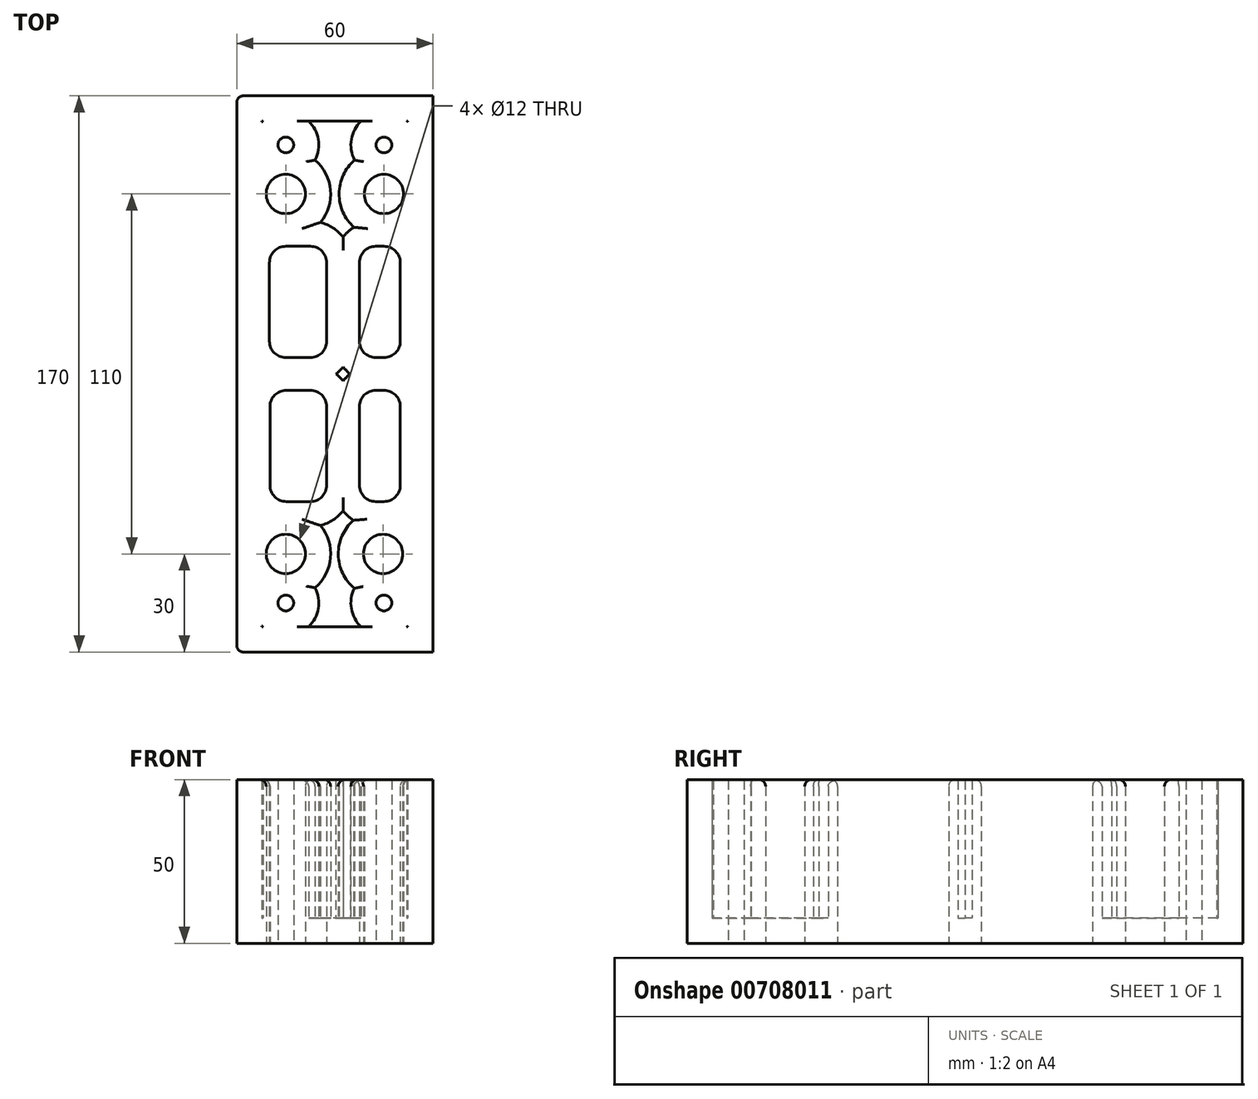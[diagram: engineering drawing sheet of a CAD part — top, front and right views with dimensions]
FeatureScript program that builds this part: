
annotation { "Feature Type Name" : "Feature", "Feature Type Description" : "" }
export const myFeature = defineFeature(function(context is Context, id is Id, definition is map)
    precondition{}
    {
        {
            var Q0;
            Q0=qCreatedBy(makeId("Top.planeOp"),FACE);
            var sketch = newSketch(context, id + "F0", { "sketchPlane" : qUnion([Q0])});
            skLineSegment(sketch, "E0.bottom", {"start": v(0, 0) * mm, "end": v(-55, 0) * mm});
            skLineSegment(sketch, "E0.top", {"start": v(0, 170) * mm, "end": v(-55, 170) * mm});
            skLineSegment(sketch, "E0.left", {"start": v(0, 0) * mm, "end": v(0, 170) * mm});
            skLineSegment(sketch, "E1.bottom", {"start": v(-55, 0) * mm, "end": v(-60, 0) * mm});
            skLineSegment(sketch, "E1.top", {"start": v(-55, 170) * mm, "end": v(-60, 170) * mm});
            skLineSegment(sketch, "E1.right", {"start": v(-60, 0) * mm, "end": v(-60, 170) * mm});
            skLineSegment(sketch, "E2.bottom", {"start": v(-55, 170) * mm, "end": v(-45, 170) * mm});
            skLineSegment(sketch, "E2.top", {"start": v(-60, 155) * mm, "end": v(-45, 155) * mm, "construction": true});
            skLineSegment(sketch, "E2.right", {"start": v(-45, 170) * mm, "end": v(-45, 155) * mm, "construction": true});
            skLineSegment(sketch, "E3.bottom", {"start": v(0, 170) * mm, "end": v(-15, 170) * mm});
            skLineSegment(sketch, "E3.top", {"start": v(0, 155) * mm, "end": v(-15, 155) * mm, "construction": true});
            skLineSegment(sketch, "E3.left", {"start": v(0, 170) * mm, "end": v(0, 155) * mm});
            skLineSegment(sketch, "E3.right", {"start": v(-15, 170) * mm, "end": v(-15, 155) * mm, "construction": true});
            skLineSegment(sketch, "E4.bottom", {"start": v(0, 0) * mm, "end": v(-15, 0) * mm});
            skLineSegment(sketch, "E4.top", {"start": v(0, 15) * mm, "end": v(-15, 15) * mm, "construction": true});
            skLineSegment(sketch, "E4.left", {"start": v(0, 0) * mm, "end": v(0, 15) * mm});
            skLineSegment(sketch, "E4.right", {"start": v(-15, 0) * mm, "end": v(-15, 15) * mm, "construction": true});
            skLineSegment(sketch, "E5.bottom", {"start": v(-55, 0) * mm, "end": v(-45, 0) * mm});
            skLineSegment(sketch, "E5.top", {"start": v(-55, 15) * mm, "end": v(-45, 15) * mm, "construction": true});
            skLineSegment(sketch, "E5.right", {"start": v(-45, 0) * mm, "end": v(-45, 15) * mm, "construction": true});
            skCircle(sketch, "E6", {"center": v(-45, 15) * mm, "radius": 2.4 * mm});
            skCircle(sketch, "E7", {"center": v(-15, 15) * mm, "radius": 2.4 * mm});
            skCircle(sketch, "E8", {"center": v(-15, 155) * mm, "radius": 2.4 * mm});
            skCircle(sketch, "E9", {"center": v(-45, 155) * mm, "radius": 2.4 * mm});
            skLineSegment(sketch, "E10", {"start": v(-45, 155) * mm, "end": v(-45, 140) * mm, "construction": true});
            skLineSegment(sketch, "E11", {"start": v(-15, 155) * mm, "end": v(-15, 140) * mm, "construction": true});
            skLineSegment(sketch, "E12", {"start": v(-45, 15) * mm, "end": v(-45, 30) * mm, "construction": true});
            skLineSegment(sketch, "E13", {"start": v(-15, 15) * mm, "end": v(-15.26, 30) * mm, "construction": true});
            skCircle(sketch, "E14", {"center": v(-45, 30) * mm, "radius": 6 * mm});
            skCircle(sketch, "E15", {"center": v(-15.26, 30) * mm, "radius": 6 * mm});
            skCircle(sketch, "E16", {"center": v(-45, 140) * mm, "radius": 6 * mm});
            skCircle(sketch, "E17", {"center": v(-15, 140) * mm, "radius": 6 * mm});
            skLineSegment(sketch, "E18", {"start": v(-27.5, 170) * mm, "end": v(-27.5, 0) * mm, "construction": true});
            skLineSegment(sketch, "E19.0", {"start": v(-32.5, 119) * mm, "end": v(-32.5, 95) * mm});
            skLineSegment(sketch, "E20.0", {"start": v(-22.5, 119) * mm, "end": v(-22.5, 95) * mm});
            skLineSegment(sketch, "E21", {"start": v(-55, 85) * mm, "end": v(0, 85) * mm, "construction": true});
            skLineSegment(sketch, "E22.0", {"start": v(-44.84, 80) * mm, "end": v(-37.5, 80) * mm});
            skLineSegment(sketch, "E23.0", {"start": v(-45, 90) * mm, "end": v(-37.5, 90) * mm});
            skLineSegment(sketch, "E24.trimOffspring", {"start": v(-17.5, 90) * mm, "end": v(-15, 90) * mm});
            skLineSegment(sketch, "E25.trimOffspring", {"start": v(-22.5, 75) * mm, "end": v(-22.5, 51) * mm});
            skLineSegment(sketch, "E26.trimOffspring", {"start": v(-17.5, 80) * mm, "end": v(-15, 80) * mm});
            skLineSegment(sketch, "E27.trimOffspring", {"start": v(-32.5, 75) * mm, "end": v(-32.5, 51) * mm});
            skLineSegment(sketch, "E28", {"start": v(-44.66, 134) * mm, "end": v(-44.66, 124) * mm, "construction": true});
            skLineSegment(sketch, "E29", {"start": v(-44.73, 36) * mm, "end": v(-44.73, 46) * mm, "construction": true});
            skLineSegment(sketch, "E30", {"start": v(-44.84, 46) * mm, "end": v(-37.5, 46) * mm});
            skLineSegment(sketch, "E31", {"start": v(-45, 124) * mm, "end": v(-37.5, 124) * mm});
            skLineSegment(sketch, "E32.trimOffspring", {"start": v(-17.5, 124) * mm, "end": v(-15, 124) * mm});
            skPoint(sketch, "E33.start.orphan", {"position": v(-15.26, 36) * mm});
            skLineSegment(sketch, "E34.trimOffspring", {"start": v(-17.5, 46) * mm, "end": v(-15, 46) * mm});
            skPoint(sketch, "E35.orphan", {"position": v(-55, 124) * mm});
            skPoint(sketch, "E36.orphan", {"position": v(-54.84, 46) * mm});
            skLineSegment(sketch, "E37.trimOffspring", {"start": v(-50, 95) * mm, "end": v(-50, 119) * mm});
            skLineSegment(sketch, "E38.trimOffspring", {"start": v(-49.84, 51) * mm, "end": v(-49.84, 75) * mm});
            skLineSegment(sketch, "E39", {"start": v(-10, 119) * mm, "end": v(-10, 95) * mm});
            skLineSegment(sketch, "E40.trimOffspring", {"start": v(-10, 75) * mm, "end": v(-10, 51) * mm});
            skPoint(sketch, "E41.visualSharp", {"position": v(-50, 124) * mm});
            skArc(sketch, "E41.filletArc", {"start": v(-45, 124) * mm, "mid": v(-48.54, 122.54) * mm, "end": v(-50, 119) * mm});
            skPoint(sketch, "E42.visualSharp", {"position": v(-32.5, 124) * mm});
            skArc(sketch, "E42.filletArc", {"start": v(-32.5, 119) * mm, "mid": v(-33.96, 122.54) * mm, "end": v(-37.5, 124) * mm});
            skPoint(sketch, "E43.visualSharp", {"position": v(-32.5, 90) * mm});
            skArc(sketch, "E43.filletArc", {"start": v(-37.5, 90) * mm, "mid": v(-33.96, 91.46) * mm, "end": v(-32.5, 95) * mm});
            skPoint(sketch, "E44.visualSharp", {"position": v(-50, 90) * mm});
            skArc(sketch, "E44.filletArc", {"start": v(-50, 95) * mm, "mid": v(-48.54, 91.46) * mm, "end": v(-45, 90) * mm});
            skPoint(sketch, "E45.visualSharp", {"position": v(-22.5, 124) * mm});
            skArc(sketch, "E45.filletArc", {"start": v(-17.5, 124) * mm, "mid": v(-21.04, 122.54) * mm, "end": v(-22.5, 119) * mm});
            skPoint(sketch, "E46.visualSharp", {"position": v(-10, 124) * mm});
            skArc(sketch, "E46.filletArc", {"start": v(-10, 119) * mm, "mid": v(-11.46, 122.54) * mm, "end": v(-15, 124) * mm});
            skPoint(sketch, "E47.visualSharp", {"position": v(-10, 90) * mm});
            skArc(sketch, "E47.filletArc", {"start": v(-15, 90) * mm, "mid": v(-11.46, 91.46) * mm, "end": v(-10, 95) * mm});
            skPoint(sketch, "E48.visualSharp", {"position": v(-22.5, 90) * mm});
            skArc(sketch, "E48.filletArc", {"start": v(-22.5, 95) * mm, "mid": v(-21.04, 91.46) * mm, "end": v(-17.5, 90) * mm});
            skPoint(sketch, "E49.visualSharp", {"position": v(-49.84, 80) * mm});
            skArc(sketch, "E49.filletArc", {"start": v(-44.84, 80) * mm, "mid": v(-48.38, 78.54) * mm, "end": v(-49.84, 75) * mm});
            skPoint(sketch, "E50.visualSharp", {"position": v(-32.5, 80) * mm});
            skArc(sketch, "E50.filletArc", {"start": v(-32.5, 75) * mm, "mid": v(-33.96, 78.54) * mm, "end": v(-37.5, 80) * mm});
            skPoint(sketch, "E51.visualSharp", {"position": v(-22.5, 80) * mm});
            skArc(sketch, "E51.filletArc", {"start": v(-17.5, 80) * mm, "mid": v(-21.04, 78.54) * mm, "end": v(-22.5, 75) * mm});
            skPoint(sketch, "E52.visualSharp", {"position": v(-10, 80) * mm});
            skArc(sketch, "E52.filletArc", {"start": v(-10, 75) * mm, "mid": v(-11.46, 78.54) * mm, "end": v(-15, 80) * mm});
            skPoint(sketch, "E53.visualSharp", {"position": v(-22.5, 46) * mm});
            skArc(sketch, "E53.filletArc", {"start": v(-22.5, 51) * mm, "mid": v(-21.04, 47.46) * mm, "end": v(-17.5, 46) * mm});
            skPoint(sketch, "E54.visualSharp", {"position": v(-10, 46) * mm});
            skArc(sketch, "E54.filletArc", {"start": v(-15, 46) * mm, "mid": v(-11.46, 47.46) * mm, "end": v(-10, 51) * mm});
            skPoint(sketch, "E55.visualSharp", {"position": v(-32.5, 46) * mm});
            skArc(sketch, "E55.filletArc", {"start": v(-37.5, 46) * mm, "mid": v(-33.96, 47.46) * mm, "end": v(-32.5, 51) * mm});
            skPoint(sketch, "E56.visualSharp", {"position": v(-49.84, 46) * mm});
            skArc(sketch, "E56.filletArc", {"start": v(-49.84, 51) * mm, "mid": v(-48.38, 47.46) * mm, "end": v(-44.84, 46) * mm});
            skSolve(sketch);
        }
        {
            var Q0;
            Q0 = qSketchRegion(id + "F0", true);
            extrude(context, id + "F1", {"entities" : qUnion([Q0]), "depth" : 50 * mm, "offsetDistance" : 25 * mm});
        }
        {
            var Q0;
            Q0=makeQuery(id+"F1.opExtrude","CAP_FACE",FACE,{"disambiguationData":[OSD([sQuery(id+"F0.wireOp",EDGE,"E0.bottom"),sQuery(id+"F0.wireOp",EDGE,"E0.top"),sQuery(id+"F0.wireOp",EDGE,"E0.left"),sQuery(id+"F0.wireOp",EDGE,"E1.bottom"),sQuery(id+"F0.wireOp",EDGE,"E1.top"),sQuery(id+"F0.wireOp",EDGE,"E1.right"),sQuery(id+"F0.wireOp",EDGE,"E2.bottom"),sQuery(id+"F0.wireOp",EDGE,"E3.bottom"),sQuery(id+"F0.wireOp",EDGE,"E3.left"),sQuery(id+"F0.wireOp",EDGE,"E4.bottom"),sQuery(id+"F0.wireOp",EDGE,"E4.left"),sQuery(id+"F0.wireOp",EDGE,"E5.bottom"),sQuery(id+"F0.wireOp",EDGE,"E6"),sQuery(id+"F0.wireOp",EDGE,"E7"),sQuery(id+"F0.wireOp",EDGE,"E8"),sQuery(id+"F0.wireOp",EDGE,"E9"),sQuery(id+"F0.wireOp",EDGE,"E14"),sQuery(id+"F0.wireOp",EDGE,"E15"),sQuery(id+"F0.wireOp",EDGE,"E16"),sQuery(id+"F0.wireOp",EDGE,"E17"),sQuery(id+"F0.wireOp",EDGE,"E19.0"),sQuery(id+"F0.wireOp",EDGE,"E20.0"),sQuery(id+"F0.wireOp",EDGE,"E22.0"),sQuery(id+"F0.wireOp",EDGE,"E23.0"),sQuery(id+"F0.wireOp",EDGE,"E24.trimOffspring"),sQuery(id+"F0.wireOp",EDGE,"E25.trimOffspring"),sQuery(id+"F0.wireOp",EDGE,"E26.trimOffspring"),sQuery(id+"F0.wireOp",EDGE,"E27.trimOffspring"),sQuery(id+"F0.wireOp",EDGE,"E30"),sQuery(id+"F0.wireOp",EDGE,"E31"),sQuery(id+"F0.wireOp",EDGE,"E32.trimOffspring"),sQuery(id+"F0.wireOp",EDGE,"E34.trimOffspring"),sQuery(id+"F0.wireOp",EDGE,"E37.trimOffspring"),sQuery(id+"F0.wireOp",EDGE,"E38.trimOffspring"),sQuery(id+"F0.wireOp",EDGE,"E39"),sQuery(id+"F0.wireOp",EDGE,"E40.trimOffspring"),sQuery(id+"F0.wireOp",EDGE,"E41.filletArc"),sQuery(id+"F0.wireOp",EDGE,"E42.filletArc"),sQuery(id+"F0.wireOp",EDGE,"E43.filletArc"),sQuery(id+"F0.wireOp",EDGE,"E44.filletArc"),sQuery(id+"F0.wireOp",EDGE,"E45.filletArc"),sQuery(id+"F0.wireOp",EDGE,"E46.filletArc"),sQuery(id+"F0.wireOp",EDGE,"E47.filletArc"),sQuery(id+"F0.wireOp",EDGE,"E48.filletArc"),sQuery(id+"F0.wireOp",EDGE,"E49.filletArc"),sQuery(id+"F0.wireOp",EDGE,"E50.filletArc"),sQuery(id+"F0.wireOp",EDGE,"E51.filletArc"),sQuery(id+"F0.wireOp",EDGE,"E52.filletArc"),sQuery(id+"F0.wireOp",EDGE,"E53.filletArc"),sQuery(id+"F0.wireOp",EDGE,"E54.filletArc"),sQuery(id+"F0.wireOp",EDGE,"E55.filletArc"),sQuery(id+"F0.wireOp",EDGE,"E56.filletArc")])],"isStart":false});
            shell(context, id + "F2", {"entities" : qUnion([Q0]), "thickness" : 7.7 * mm});
        }
        {
            var Q0;
            Q0=makeQuery(id+"F1.opExtrude","SWEPT_EDGE",EDGE,{"disambiguationData":[OSD([sQuery(id+"F0.wireOp",EDGE,"E1.bottom"),sQuery(id+"F0.wireOp",EDGE,"E1.right")])]});
            var Q1;
            Q1=makeQuery(id+"F1.opExtrude","SWEPT_EDGE",EDGE,{"disambiguationData":[OSD([sQuery(id+"F0.wireOp",EDGE,"E4.bottom"),sQuery(id+"F0.wireOp",EDGE,"E4.left")])]});
            var Q2;
            Q2=makeQuery(id+"F1.opExtrude","SWEPT_EDGE",EDGE,{"disambiguationData":[OSD([sQuery(id+"F0.wireOp",EDGE,"E3.bottom"),sQuery(id+"F0.wireOp",EDGE,"E3.left")])]});
            var Q3;
            Q3=makeQuery(id+"F1.opExtrude","SWEPT_EDGE",EDGE,{"disambiguationData":[OSD([sQuery(id+"F0.wireOp",EDGE,"E1.top"),sQuery(id+"F0.wireOp",EDGE,"E1.right")])]});
            fillet(context, id + "F3", {"entities" : qUnion([Q0, Q1, Q2, Q3]), "radius" : 2 * mm, "tangentPropagation" : true, "allowEdgeOverflow" : false});
        }
        {
            var Q0;
            {var subQ0=sQuery(id+"F0.wireOp",EDGE,"E8");Q0=makeQuery(id+"F2.opShell","OFFSET_EDGE",EDGE,{"disambiguationData":[OSD([subQ0]),TDD([makeQuery(id+"F1.opExtrude","CAP_EDGE",EDGE,{"disambiguationData":[OSD([subQ0])],"isStart":false})]),OD(1.0)]});}
            var Q1;
            {var subQ0=sQuery(id+"F0.wireOp",EDGE,"E17");Q1=makeQuery(id+"F2.opShell","OFFSET_EDGE",EDGE,{"disambiguationData":[OSD([subQ0]),TDD([makeQuery(id+"F1.opExtrude","CAP_EDGE",EDGE,{"disambiguationData":[OSD([subQ0])],"isStart":false})])]});}
            var Q2;
            {var subQ0=sQuery(id+"F0.wireOp",EDGE,"E16");Q2=makeQuery(id+"F2.opShell","OFFSET_EDGE",EDGE,{"disambiguationData":[OSD([subQ0]),TDD([makeQuery(id+"F1.opExtrude","CAP_EDGE",EDGE,{"disambiguationData":[OSD([subQ0])],"isStart":false})])]});}
            var Q3;
            {var subQ0=sQuery(id+"F0.wireOp",EDGE,"E42.filletArc");Q3=makeQuery(id+"F2.opShell","OFFSET_EDGE",EDGE,{"disambiguationData":[OSD([subQ0]),TDD([makeQuery(id+"F1.opExtrude","CAP_EDGE",EDGE,{"disambiguationData":[OSD([subQ0])],"isStart":false})])]});}
            var Q4;
            {var subQ0=sQuery(id+"F0.wireOp",EDGE,"E45.filletArc");Q4=makeQuery(id+"F2.opShell","OFFSET_EDGE",EDGE,{"disambiguationData":[OSD([subQ0]),TDD([makeQuery(id+"F1.opExtrude","CAP_EDGE",EDGE,{"disambiguationData":[OSD([subQ0])],"isStart":false})])]});}
            var Q5;
            Q5=makeQuery(id+"F1.opExtrude","CAP_EDGE",EDGE,{"disambiguationData":[OSD([sQuery(id+"F0.wireOp",EDGE,"E32.trimOffspring")])],"isStart":false});
            var Q6;
            Q6=makeQuery(id+"F1.opExtrude","CAP_EDGE",EDGE,{"disambiguationData":[OSD([sQuery(id+"F0.wireOp",EDGE,"E46.filletArc")])],"isStart":false});
            var Q7;
            Q7=makeQuery(id+"F1.opExtrude","CAP_EDGE",EDGE,{"disambiguationData":[OSD([sQuery(id+"F0.wireOp",EDGE,"E45.filletArc")])],"isStart":false});
            var Q8;
            Q8=makeQuery(id+"F1.opExtrude","CAP_EDGE",EDGE,{"disambiguationData":[OSD([sQuery(id+"F0.wireOp",EDGE,"E20.0")])],"isStart":false});
            var Q9;
            Q9=makeQuery(id+"F1.opExtrude","CAP_EDGE",EDGE,{"disambiguationData":[OSD([sQuery(id+"F0.wireOp",EDGE,"E39")])],"isStart":false});
            var Q10;
            Q10=makeQuery(id+"F1.opExtrude","CAP_EDGE",EDGE,{"disambiguationData":[OSD([sQuery(id+"F0.wireOp",EDGE,"E47.filletArc")])],"isStart":false});
            var Q11;
            Q11=makeQuery(id+"F1.opExtrude","CAP_EDGE",EDGE,{"disambiguationData":[OSD([sQuery(id+"F0.wireOp",EDGE,"E24.trimOffspring")])],"isStart":false});
            var Q12;
            Q12=makeQuery(id+"F1.opExtrude","CAP_EDGE",EDGE,{"disambiguationData":[OSD([sQuery(id+"F0.wireOp",EDGE,"E48.filletArc")])],"isStart":false});
            var Q13;
            Q13=makeQuery(id+"F1.opExtrude","CAP_EDGE",EDGE,{"disambiguationData":[OSD([sQuery(id+"F0.wireOp",EDGE,"E19.0")])],"isStart":false});
            var Q14;
            Q14=makeQuery(id+"F1.opExtrude","CAP_EDGE",EDGE,{"disambiguationData":[OSD([sQuery(id+"F0.wireOp",EDGE,"E42.filletArc")])],"isStart":false});
            var Q15;
            Q15=makeQuery(id+"F1.opExtrude","CAP_EDGE",EDGE,{"disambiguationData":[OSD([sQuery(id+"F0.wireOp",EDGE,"E31")])],"isStart":false});
            var Q16;
            Q16=makeQuery(id+"F1.opExtrude","CAP_EDGE",EDGE,{"disambiguationData":[OSD([sQuery(id+"F0.wireOp",EDGE,"E41.filletArc")])],"isStart":false});
            var Q17;
            Q17=makeQuery(id+"F1.opExtrude","CAP_EDGE",EDGE,{"disambiguationData":[OSD([sQuery(id+"F0.wireOp",EDGE,"E37.trimOffspring")])],"isStart":false});
            var Q18;
            Q18=makeQuery(id+"F1.opExtrude","CAP_EDGE",EDGE,{"disambiguationData":[OSD([sQuery(id+"F0.wireOp",EDGE,"E44.filletArc")])],"isStart":false});
            var Q19;
            Q19=makeQuery(id+"F1.opExtrude","CAP_EDGE",EDGE,{"disambiguationData":[OSD([sQuery(id+"F0.wireOp",EDGE,"E23.0")])],"isStart":false});
            var Q20;
            Q20=makeQuery(id+"F1.opExtrude","CAP_EDGE",EDGE,{"disambiguationData":[OSD([sQuery(id+"F0.wireOp",EDGE,"E43.filletArc")])],"isStart":false});
            var Q21;
            Q21=makeQuery(id+"F1.opExtrude","CAP_EDGE",EDGE,{"disambiguationData":[OSD([sQuery(id+"F0.wireOp",EDGE,"E26.trimOffspring")])],"isStart":false});
            var Q22;
            Q22=makeQuery(id+"F1.opExtrude","CAP_EDGE",EDGE,{"disambiguationData":[OSD([sQuery(id+"F0.wireOp",EDGE,"E51.filletArc")])],"isStart":false});
            var Q23;
            Q23=makeQuery(id+"F1.opExtrude","CAP_EDGE",EDGE,{"disambiguationData":[OSD([sQuery(id+"F0.wireOp",EDGE,"E52.filletArc")])],"isStart":false});
            var Q24;
            Q24=makeQuery(id+"F1.opExtrude","CAP_EDGE",EDGE,{"disambiguationData":[OSD([sQuery(id+"F0.wireOp",EDGE,"E40.trimOffspring")])],"isStart":false});
            var Q25;
            Q25=makeQuery(id+"F1.opExtrude","CAP_EDGE",EDGE,{"disambiguationData":[OSD([sQuery(id+"F0.wireOp",EDGE,"E25.trimOffspring")])],"isStart":false});
            var Q26;
            Q26=makeQuery(id+"F1.opExtrude","CAP_EDGE",EDGE,{"disambiguationData":[OSD([sQuery(id+"F0.wireOp",EDGE,"E34.trimOffspring")])],"isStart":false});
            var Q27;
            Q27=makeQuery(id+"F1.opExtrude","CAP_EDGE",EDGE,{"disambiguationData":[OSD([sQuery(id+"F0.wireOp",EDGE,"E54.filletArc")])],"isStart":false});
            var Q28;
            Q28=makeQuery(id+"F1.opExtrude","CAP_EDGE",EDGE,{"disambiguationData":[OSD([sQuery(id+"F0.wireOp",EDGE,"E53.filletArc")])],"isStart":false});
            var Q29;
            Q29=makeQuery(id+"F1.opExtrude","CAP_EDGE",EDGE,{"disambiguationData":[OSD([sQuery(id+"F0.wireOp",EDGE,"E27.trimOffspring")])],"isStart":false});
            var Q30;
            Q30=makeQuery(id+"F1.opExtrude","CAP_EDGE",EDGE,{"disambiguationData":[OSD([sQuery(id+"F0.wireOp",EDGE,"E38.trimOffspring")])],"isStart":false});
            var Q31;
            Q31=makeQuery(id+"F1.opExtrude","CAP_EDGE",EDGE,{"disambiguationData":[OSD([sQuery(id+"F0.wireOp",EDGE,"E22.0")])],"isStart":false});
            var Q32;
            Q32=makeQuery(id+"F1.opExtrude","CAP_EDGE",EDGE,{"disambiguationData":[OSD([sQuery(id+"F0.wireOp",EDGE,"E30")])],"isStart":false});
            var Q33;
            Q33=makeQuery(id+"F1.opExtrude","CAP_EDGE",EDGE,{"disambiguationData":[OSD([sQuery(id+"F0.wireOp",EDGE,"E55.filletArc")])],"isStart":false});
            var Q34;
            Q34=makeQuery(id+"F1.opExtrude","CAP_EDGE",EDGE,{"disambiguationData":[OSD([sQuery(id+"F0.wireOp",EDGE,"E50.filletArc")])],"isStart":false});
            var Q35;
            Q35=makeQuery(id+"F1.opExtrude","CAP_EDGE",EDGE,{"disambiguationData":[OSD([sQuery(id+"F0.wireOp",EDGE,"E49.filletArc")])],"isStart":false});
            var Q36;
            Q36=makeQuery(id+"F1.opExtrude","CAP_EDGE",EDGE,{"disambiguationData":[OSD([sQuery(id+"F0.wireOp",EDGE,"E56.filletArc")])],"isStart":false});
            var Q37;
            {var subQ0=sQuery(id+"F0.wireOp",EDGE,"E7");Q37=makeQuery(id+"F2.opShell","OFFSET_EDGE",EDGE,{"disambiguationData":[OSD([subQ0]),TDD([makeQuery(id+"F1.opExtrude","CAP_EDGE",EDGE,{"disambiguationData":[OSD([subQ0])],"isStart":false})]),OD(1.0)]});}
            var Q38;
            {var subQ0=sQuery(id+"F0.wireOp",EDGE,"E14");Q38=makeQuery(id+"F2.opShell","OFFSET_EDGE",EDGE,{"disambiguationData":[OSD([subQ0]),TDD([makeQuery(id+"F1.opExtrude","CAP_EDGE",EDGE,{"disambiguationData":[OSD([subQ0])],"isStart":false})])]});}
            var Q39;
            {var subQ0=sQuery(id+"F0.wireOp",EDGE,"E15");Q39=makeQuery(id+"F2.opShell","OFFSET_EDGE",EDGE,{"disambiguationData":[OSD([subQ0]),TDD([makeQuery(id+"F1.opExtrude","CAP_EDGE",EDGE,{"disambiguationData":[OSD([subQ0])],"isStart":false})])]});}
            var Q40;
            {var subQ0=sQuery(id+"F0.wireOp",EDGE,"E53.filletArc");Q40=makeQuery(id+"F2.opShell","OFFSET_EDGE",EDGE,{"disambiguationData":[OSD([subQ0]),TDD([makeQuery(id+"F1.opExtrude","CAP_EDGE",EDGE,{"disambiguationData":[OSD([subQ0])],"isStart":false})])]});}
            var Q41;
            {var subQ0=sQuery(id+"F0.wireOp",EDGE,"E55.filletArc");Q41=makeQuery(id+"F2.opShell","OFFSET_EDGE",EDGE,{"disambiguationData":[OSD([subQ0]),TDD([makeQuery(id+"F1.opExtrude","CAP_EDGE",EDGE,{"disambiguationData":[OSD([subQ0])],"isStart":false})])]});}
            var Q42;
            {var subQ0=sQuery(id+"F0.wireOp",EDGE,"E6");Q42=makeQuery(id+"F2.opShell","OFFSET_EDGE",EDGE,{"disambiguationData":[OSD([subQ0]),TDD([makeQuery(id+"F1.opExtrude","CAP_EDGE",EDGE,{"disambiguationData":[OSD([subQ0])],"isStart":false})]),OD(1.0)]});}
            var Q43;
            {var subQ0=sQuery(id+"F0.wireOp",EDGE,"E9");Q43=makeQuery(id+"F2.opShell","OFFSET_EDGE",EDGE,{"disambiguationData":[OSD([subQ0]),TDD([makeQuery(id+"F1.opExtrude","CAP_EDGE",EDGE,{"disambiguationData":[OSD([subQ0])],"isStart":false})]),OD(1.0)]});}
            var Q44;
            Q44=makeQuery(id+"F1.opExtrude","CAP_EDGE",EDGE,{"disambiguationData":[OSD([sQuery(id+"F0.wireOp",EDGE,"E17")])],"isStart":false});
            var Q45;
            Q45=makeQuery(id+"F1.opExtrude","CAP_EDGE",EDGE,{"disambiguationData":[OSD([sQuery(id+"F0.wireOp",EDGE,"E16")])],"isStart":false});
            var Q46;
            Q46=makeQuery(id+"F1.opExtrude","CAP_EDGE",EDGE,{"disambiguationData":[OSD([sQuery(id+"F0.wireOp",EDGE,"E15")])],"isStart":false});
            var Q47;
            Q47=makeQuery(id+"F1.opExtrude","CAP_EDGE",EDGE,{"disambiguationData":[OSD([sQuery(id+"F0.wireOp",EDGE,"E14")])],"isStart":false});
            fillet(context, id + "F4", {"entities" : qUnion([Q0, Q1, Q2, Q3, Q4, Q5, Q6, Q7, Q8, Q9, Q10, Q11, Q12, Q13, Q14, Q15, Q16, Q17, Q18, Q19, Q20, Q21, Q22, Q23, Q24, Q25, Q26, Q27, Q28, Q29, Q30, Q31, Q32, Q33, Q34, Q35, Q36, Q37, Q38, Q39, Q40, Q41, Q42, Q43, Q44, Q45, Q46, Q47]), "radius" : 2 * mm, "tangentPropagation" : true, "allowEdgeOverflow" : false});
        }
    });
